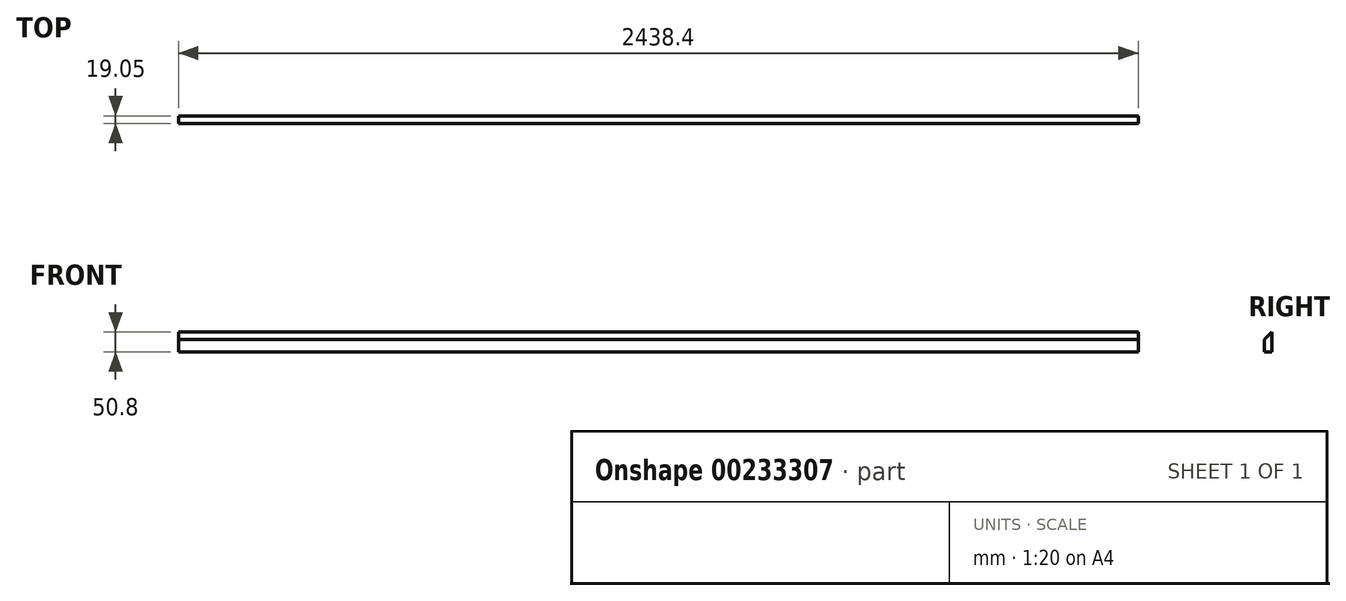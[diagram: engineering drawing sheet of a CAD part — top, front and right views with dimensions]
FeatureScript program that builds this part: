
annotation { "Feature Type Name" : "Feature", "Feature Type Description" : "" }
export const myFeature = defineFeature(function(context is Context, id is Id, definition is map)
    precondition{}
    {
        {
            var Q0;
            Q0=qCreatedBy(makeId("Right.planeOp"),FACE);
            var sketch = newSketch(context, id + "F0", { "sketchPlane" : qUnion([Q0])});
            skLineSegment(sketch, "E0.bottom", {"start": v(0, 0) * mm, "end": v(19.05, 0) * mm});
            skLineSegment(sketch, "E0.left", {"start": v(0, 0) * mm, "end": v(0, 31.75) * mm});
            skLineSegment(sketch, "E0.right", {"start": v(19.05, 0) * mm, "end": v(19.05, 50.8) * mm});
            skLineSegment(sketch, "E1", {"start": v(19.05, 50.8) * mm, "end": v(0, 31.75) * mm});
            skSolve(sketch);
        }
        {
            var Q0;
            Q0 = qSketchRegion(id + "F0", true);
            extrude(context, id + "F1", {"entities" : qUnion([Q0]), "depth" : 2438.4 * mm});
        }
    });
